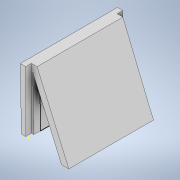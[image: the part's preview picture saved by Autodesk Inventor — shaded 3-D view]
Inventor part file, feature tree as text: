
AUTODESK INVENTOR PART (.ipt)
format: ipt  version: 2020 (Build 240168000, 168)  size: 194,560 bytes
history: native  units: in
note: dims shown in document units (in); Inventor stores cm internally (conversion verified against a paired STEP export)
features: sketch x7, extrude x4, draft x1, shell x1, sweep x1
ambient origin geometry x8: Origin, YZ Plane, XZ Plane, XY Plane, X Axis, Y Axis, Z Axis, Center Point
bodies: Body1 (feature_tree)
feature tree (14):
  extrude  "Extrusion7"  Depth=0.0669in
  draft  "FaceDraft6"
  shell  "Shell6"  Thickness=0.0669in
  sketch  "Sketch19"  dims[d60=1.1339in d61=0.0669in]
  sketch  "Sketch20"  dims[d62=0.0669in d63=0.7205in d64=0.0034in]
  extrude  "Extrusion15"  Depth=0.0669in
  extrude  "Extrusion16"  Depth=0.7205in
  sweep  "Sweep1"
  extrude  "Extrusion17"  Depth=0.0984in TaperAngle=0.0deg
  sketch  "Sketch1"  dims[d55=0.0512in d56=0.0669in d57=0.0669in]
  sketch  "Sketch21"  dims[d109=0.158in d110=0.0787in]
  sketch  "Sketch22"  dims[d113=0.0984in d114=0.0in d115=0.0984in d116=0.0in]
  sketch  "Sketch23"  dims[d117=0.1575in]
  sketch  "Sketch24"  dims[d118=0.0in d119=0.0in d120=0.5906in d121=0.0984in d122=0.0984in d123=0.0984in d124=0.2362in d125=0.0in d126=0.0984in d127=0.0984in d28=0.0197in d29=0.0344in d30=0.0197in d31=0.0344in d58=0.0197in d59=0.0344in]
